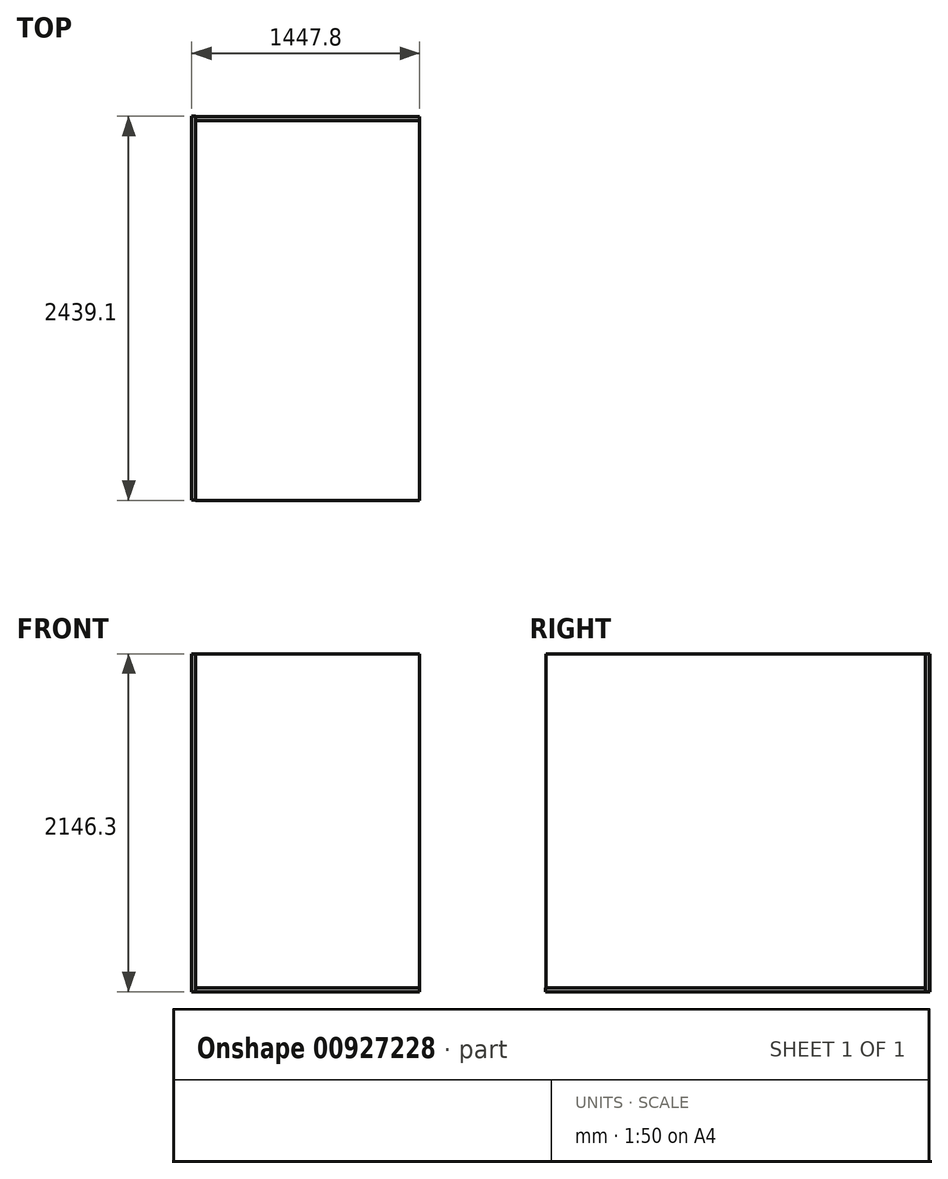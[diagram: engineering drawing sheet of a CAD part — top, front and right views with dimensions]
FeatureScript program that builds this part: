
annotation { "Feature Type Name" : "Feature", "Feature Type Description" : "" }
export const myFeature = defineFeature(function(context is Context, id is Id, definition is map)
    precondition{}
    {
        {
            var Q0;
            Q0=qCreatedBy(makeId("Top.planeOp"),FACE);
            var sketch = newSketch(context, id + "F0", { "sketchPlane" : qUnion([Q0])});
            skLineSegment(sketch, "E0.bottom", {"start": v(0, 0) * mm, "end": v(1422.4, 0) * mm});
            skLineSegment(sketch, "E0.top", {"start": v(0, -2413) * mm, "end": v(1422.4, -2413) * mm});
            skLineSegment(sketch, "E0.left", {"start": v(0, 0) * mm, "end": v(0, -2413) * mm});
            skLineSegment(sketch, "E0.right", {"start": v(1422.4, 0) * mm, "end": v(1422.4, -2413) * mm});
            skSolve(sketch);
        }
        {
            var Q0;
            Q0 = qSketchRegion(id + "F0", true);
            extrude(context, id + "F1", {"entities" : qUnion([Q0]), "depth" : 25.4 * mm, "offsetDistance" : 25.4 * mm});
        }
        {
            var Q0;
            Q0=makeQuery(id+"F1.opExtrude","CAP_FACE",FACE,{"disambiguationData":[OSD([sQuery(id+"F0.wireOp",EDGE,"E0.bottom"),sQuery(id+"F0.wireOp",EDGE,"E0.top"),sQuery(id+"F0.wireOp",EDGE,"E0.left"),sQuery(id+"F0.wireOp",EDGE,"E0.right")])],"isStart":false});
            var sketch = newSketch(context, id + "F2", { "sketchPlane" : qUnion([Q0])});
            skLineSegment(sketch, "E1.bottom", {"start": v(0, 0) * mm, "end": v(1422.4, 0) * mm});
            skLineSegment(sketch, "E1.top", {"start": v(0, 25.4) * mm, "end": v(1422.4, 25.4) * mm});
            skLineSegment(sketch, "E1.left", {"start": v(0, 0) * mm, "end": v(0, 25.4) * mm});
            skLineSegment(sketch, "E1.right", {"start": v(1422.4, 0) * mm, "end": v(1422.4, 25.4) * mm});
            skSolve(sketch);
        }
        {
            var Q0;
            Q0 = qSketchRegion(id + "F2", true);
            extrude(context, id + "F3", {"entities" : qUnion([Q0]), "depth" : 2120.9 * mm, "offsetDistance" : 25.4 * mm, "hasSecondDirection" : true, "secondDirectionOppositeDirection" : true, "secondDirectionDepth" : 25.4 * mm});
        }
        {
            var Q0;
            Q0=qCreatedBy(makeId("Top.planeOp"),FACE);
            var sketch = newSketch(context, id + "F4", { "sketchPlane" : qUnion([Q0])});
            skLineSegment(sketch, "E2.bottom", {"start": v(0, -2412.3) * mm, "end": v(-25.4, -2412.3) * mm});
            skLineSegment(sketch, "E2.top", {"start": v(0, 26.1) * mm, "end": v(-25.4, 26.1) * mm});
            skLineSegment(sketch, "E2.left", {"start": v(0, -2412.3) * mm, "end": v(0, 26.1) * mm});
            skLineSegment(sketch, "E2.right", {"start": v(-25.4, -2412.3) * mm, "end": v(-25.4, 26.1) * mm});
            skSolve(sketch);
        }
        {
            var Q0;
            Q0 = qSketchRegion(id + "F4", true);
            extrude(context, id + "F5", {"entities" : qUnion([Q0]), "depth" : 2146.3 * mm, "offsetDistance" : 25.4 * mm});
        }
    });
